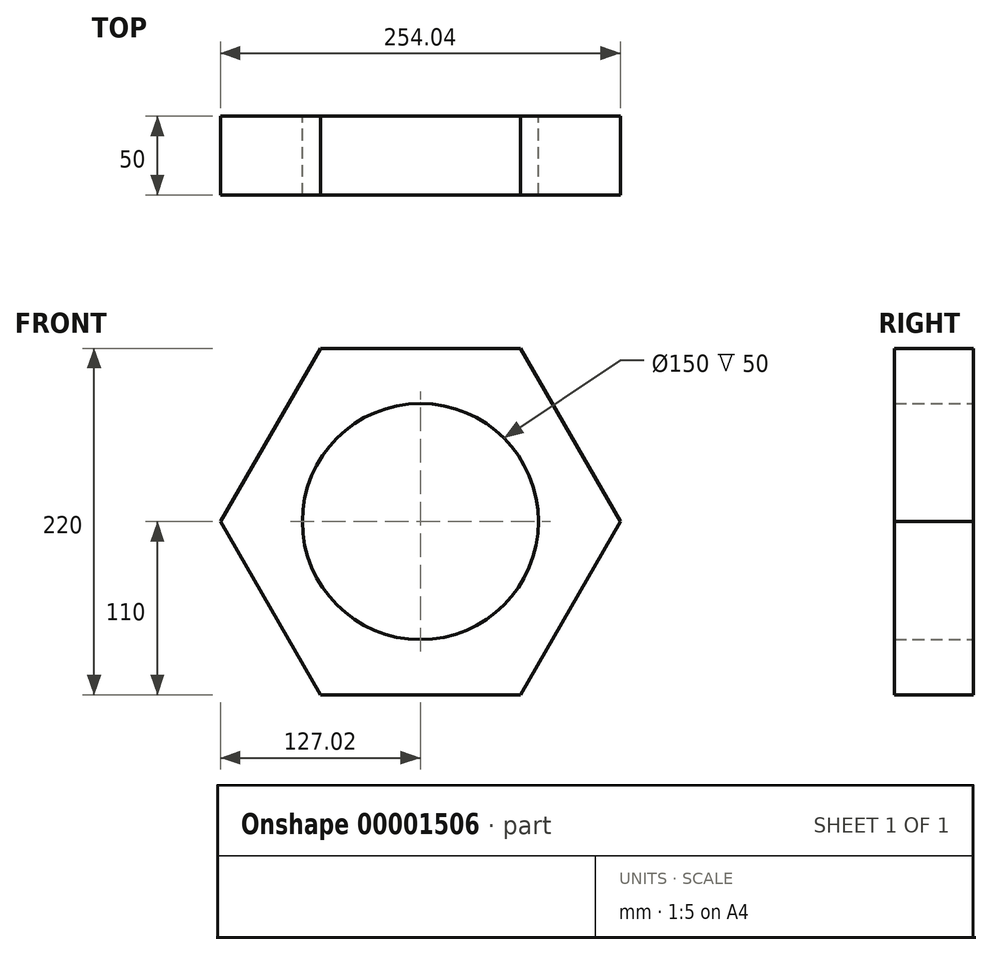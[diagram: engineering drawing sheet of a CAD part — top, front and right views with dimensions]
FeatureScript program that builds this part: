
annotation { "Feature Type Name" : "Feature", "Feature Type Description" : "" }
export const myFeature = defineFeature(function(context is Context, id is Id, definition is map)
    precondition{}
    {
        {
            var Q0;
            Q0=qCreatedBy(makeId("Front.planeOp"),FACE);
            var sketch = newSketch(context, id + "F0", { "sketchPlane" : qUnion([Q0])});
            skCircle(sketch, "E0", {"center": v(0, 0) * mm, "radius": 75 * mm});
            skCircle(sketch, "E1.cCircle", {"center": v(0, 0) * mm, "radius": 110 * mm, "construction": true});
            skLineSegment(sketch, "E1.0", {"start": v(-63.5, 110) * mm, "end": v(63.5, 110) * mm});
            skLineSegment(sketch, "E1.1", {"start": v(63.5, 110) * mm, "end": v(127.02, 0) * mm});
            skLineSegment(sketch, "E1.2", {"start": v(127.02, 0) * mm, "end": v(63.5, -110) * mm});
            skLineSegment(sketch, "E1.3", {"start": v(63.5, -110) * mm, "end": v(-63.5, -110) * mm});
            skLineSegment(sketch, "E1.4", {"start": v(-63.5, -110) * mm, "end": v(-127.02, 0) * mm});
            skLineSegment(sketch, "E1.5", {"start": v(-127.02, 0) * mm, "end": v(-63.5, 110) * mm});
            skPoint(sketch, "E1.0.midPoint", {"position": v(0, 110) * mm});
            skSolve(sketch);
        }
        {
            var Q0;
            Q0 = qSketchRegion(id + "F0", true);
            extrude(context, id + "F1", {"entities" : qUnion([Q0]), "depth" : 50 * mm, "offsetDistance" : 25 * mm});
        }
    });
